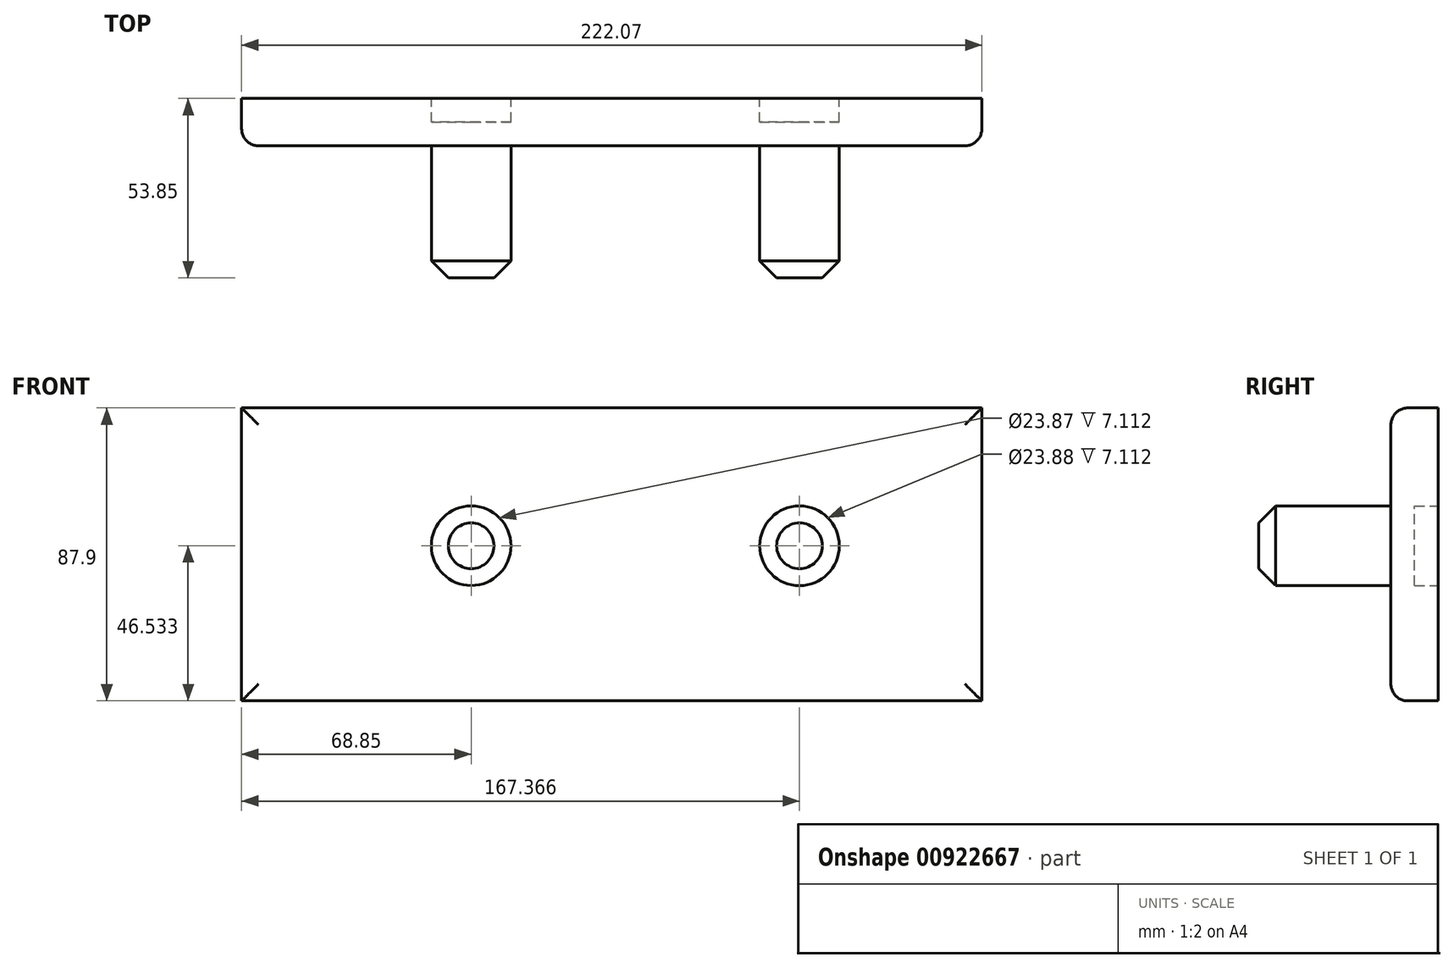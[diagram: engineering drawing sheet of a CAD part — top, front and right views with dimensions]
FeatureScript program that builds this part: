
annotation { "Feature Type Name" : "Feature", "Feature Type Description" : "" }
export const myFeature = defineFeature(function(context is Context, id is Id, definition is map)
    precondition{}
    {
        {
            var Q0;
            Q0=qCreatedBy(makeId("Front.planeOp"),FACE);
            var sketch = newSketch(context, id + "F0", { "sketchPlane" : qUnion([Q0])});
            skLineSegment(sketch, "E0.bottom", {"start": v(-102.46, 36.06) * mm, "end": v(119.6, 36.06) * mm});
            skLineSegment(sketch, "E0.top", {"start": v(-102.46, -51.84) * mm, "end": v(119.6, -51.84) * mm});
            skLineSegment(sketch, "E0.left", {"start": v(-102.46, 36.06) * mm, "end": v(-102.46, -51.84) * mm});
            skLineSegment(sketch, "E0.right", {"start": v(119.6, 36.06) * mm, "end": v(119.6, -51.84) * mm});
            skCircle(sketch, "E1", {"center": v(64.9, -5.3) * mm, "radius": 11.94 * mm});
            skCircle(sketch, "E2", {"center": v(-33.6, -5.3) * mm, "radius": 11.94 * mm});
            skSolve(sketch);
        }
        {
            var Q0;
            Q0=makeQuery(id+"F0.imprint","IMPRINT",FACE,{"disambiguationData":[TD([[makeQuery(id+"F0.imprint","IMPRINT",EDGE,{"derivedFrom":sQuery(id+"F0.wireOp",EDGE,"E0.bottom")}),-1.0]])]});
            extrude(context, id + "F1", {"entities" : qUnion([Q0]), "endBound" : BoundingType.SYMMETRIC, "depth" : 14.22 * mm, "offsetDistance" : 25.4 * mm});
        }
        {
            var Q0;
            Q0=makeQuery(id+"F1.opExtrude","CAP_EDGE",EDGE,{"disambiguationData":[OSD([sQuery(id+"F0.wireOp",EDGE,"E0.bottom")])],"isStart":false});
            var Q1;
            Q1=makeQuery(id+"F1.opExtrude","CAP_EDGE",EDGE,{"disambiguationData":[OSD([sQuery(id+"F0.wireOp",EDGE,"E0.left")])],"isStart":false});
            var Q2;
            Q2=makeQuery(id+"F1.opExtrude","CAP_EDGE",EDGE,{"disambiguationData":[OSD([sQuery(id+"F0.wireOp",EDGE,"E0.top")])],"isStart":false});
            var Q3;
            Q3=makeQuery(id+"F1.opExtrude","CAP_EDGE",EDGE,{"disambiguationData":[OSD([sQuery(id+"F0.wireOp",EDGE,"E0.right")])],"isStart":false});
            fillet(context, id + "F2", {"entities" : qUnion([Q0, Q1, Q2, Q3]), "radius" : 5.08 * mm, "tangentPropagation" : true, "allowEdgeOverflow" : false});
        }
        {
            var Q0;
            Q0=makeQuery(id+"F0.imprint","IMPRINT",FACE,{"disambiguationData":[TD([[makeQuery(id+"F0.imprint","IMPRINT",EDGE,{"derivedFrom":sQuery(id+"F0.wireOp",EDGE,"E1")}),1.0]])]});
            var Q1;
            Q1=makeQuery(id+"F0.imprint","IMPRINT",FACE,{"disambiguationData":[TD([[makeQuery(id+"F0.imprint","IMPRINT",EDGE,{"derivedFrom":sQuery(id+"F0.wireOp",EDGE,"E2")}),1.0]])]});
            extrude(context, id + "F3", {"entities" : qUnion([Q0, Q1]), "operationType" : NewBodyOperationType.ADD, "depth" : 46.74 * mm, "offsetDistance" : 25.4 * mm});
        }
        {
            var Q0;
            Q0=makeQuery(id+"F3.opExtrude","CAP_EDGE",EDGE,{"disambiguationData":[OSD([sQuery(id+"F0.wireOp",EDGE,"E2")])],"isStart":false});
            var Q1;
            Q1=makeQuery(id+"F3.opExtrude","CAP_EDGE",EDGE,{"disambiguationData":[OSD([sQuery(id+"F0.wireOp",EDGE,"E1")])],"isStart":false});
            chamfer(context, id + "F4", {"entities" : qUnion([Q0, Q1]), "width" : 5.08 * mm, "tangentPropagation" : true});
        }
    });
